# Revit family: DL4045551_Ducha_Dalia_RegaderaconBrazo_Grival
name_source: partatom
category: Plumbing Fixtures
units: mm (PartAtom-declared; Revit-internal decimal feet)

## family parameters
Always vertical = Yes
Cut with Voids When Loaded = No
Host = Wall
OmniClass Number = 23.31.15.11
OmniClass Title = Bath Shower Units
Part Type = Normal
Room Calculation Point = No
Round Connector Dimension = Use Diameter
Shared = No

## types (1)
- Type 1
    Alto = 105 mm  [stored 0.344488 ft]
    Altura Ducha = 1800 mm  [stored 5.90551 ft]
    Ancho = 84 mm  [stored 0.275591 ft]
    Capacidad de flujo = A 80 psi: 9,3 L/min.
    Creado por = BIMBAU
    Default Elevation = 0 mm  [stored 0 ft]
    Description = La regadera Dalia con tecnología de ahorro de agua minimiza el derroche ofreciendo un mayor rendimiento sin sacrificar el confort en la ducha, con chorro focalizado ofrece mayor practicidad en espacios pequeños o consumidores que buscan cobertura direccionada.nnDe estilo versátil, se puede combinar en cualquier diseño de baño, cuenta con salidas de agua flexibles que permiten una fácil limpieza y evitan la acumulación de residuos. Con acabado superior, mayor espesor en el cromado, más brillante y resistente a la corrosión.
    Fecha de creación = 07/04/2021
    Garantía = 30 Años Grival - 2 Años Cromado
    Manufacturer = Grival
    Material = Corona_Aluminio
    Model = Ducha Dalia Regadera Con Brazo
    Peso neto = 150 g. - 0,15 lb.
    Presion maxima = 125 psi (860 kPa).
    Presion minima = 20 psi (140 kPa).
    Profundidad = 179 mm  [stored 0.58727 ft]
    Referencia = DL4045551
    Temperatura de uso = 5˚C a 71˚C.
    URL = https://www.grival.com
    Vida útil = 10.000 ciclos.

note: [stored X ft] marks values corroborated as IEEE doubles in the binary element streams (Revit-internal decimal feet)

## geometry (parser evidence)
native form markers: Sweep x4
no freeform markers — native parametric forms only
